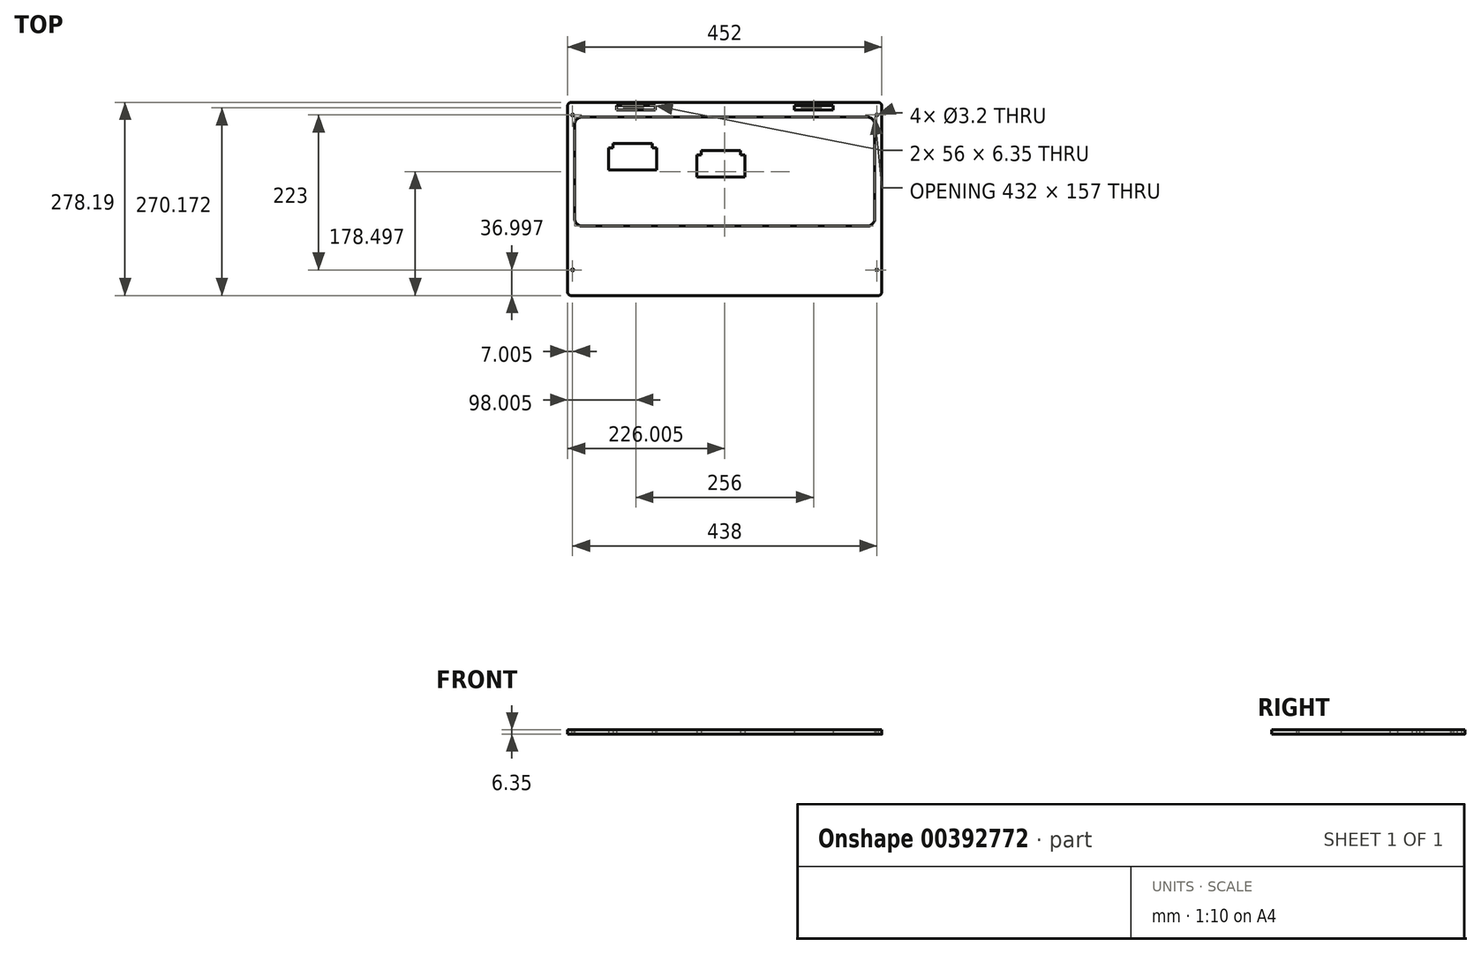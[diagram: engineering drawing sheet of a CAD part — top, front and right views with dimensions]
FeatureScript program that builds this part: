
annotation { "Feature Type Name" : "Feature", "Feature Type Description" : "" }
export const myFeature = defineFeature(function(context is Context, id is Id, definition is map)
    precondition{}
    {
        {
            var Q0;
            Q0=qCreatedBy(makeId("Top.planeOp"),FACE);
            var sketch = newSketch(context, id + "F0", { "sketchPlane" : qUnion([Q0])});
            skCircle(sketch, "E0", {"center": v(-221.69, 47.13) * mm, "radius": 1.6 * mm});
            skLineSegment(sketch, "E1", {"start": v(223.31, 49.13) * mm, "end": v(223.31, -177.87) * mm});
            skLineSegment(sketch, "E2", {"start": v(223.31, 49.13) * mm, "end": v(223.31, 47.13) * mm});
            skCircle(sketch, "E3", {"center": v(216.31, 47.13) * mm, "radius": 1.6 * mm});
            skLineSegment(sketch, "E4", {"start": v(223.31, -177.87) * mm, "end": v(223.31, -175.87) * mm});
            skLineSegment(sketch, "E5", {"start": v(-228.69, -177.87) * mm, "end": v(-228.69, -175.87) * mm});
            skCircle(sketch, "E6", {"center": v(-221.69, -175.87) * mm, "radius": 1.6 * mm});
            skCircle(sketch, "E7", {"center": v(216.31, -175.87) * mm, "radius": 1.6 * mm});
            skLineSegment(sketch, "E8", {"start": v(213.31, -31.18) * mm, "end": v(213.31, -101.87) * mm});
            skLineSegment(sketch, "E9", {"start": v(213.31, -31.18) * mm, "end": v(213.31, 33.13) * mm});
            skLineSegment(sketch, "E10", {"start": v(-207.69, -112.87) * mm, "end": v(202.31, -112.87) * mm});
            skLineSegment(sketch, "E11", {"start": v(-218.69, -34.37) * mm, "end": v(-218.69, -101.87) * mm});
            skLineSegment(sketch, "E12", {"start": v(-218.69, -34.37) * mm, "end": v(-218.69, 33.13) * mm});
            skLineSegment(sketch, "E13", {"start": v(-218.69, 33.13) * mm, "end": v(-218.69, 33.13) * mm});
            skArc(sketch, "E14.filletArc", {"start": v(-207.69, 44.13) * mm, "mid": v(-215.46, 40.9) * mm, "end": v(-218.69, 33.13) * mm});
            skArc(sketch, "E15.MirrorCS", {"start": v(202.31, 44.13) * mm, "mid": v(210.1, 40.9) * mm, "end": v(213.31, 33.13) * mm});
            skArc(sketch, "E16.MirrorCS", {"start": v(-207.69, -112.87) * mm, "mid": v(-215.46, -109.65) * mm, "end": v(-218.69, -101.87) * mm});
            skArc(sketch, "E17.MirrorCS", {"start": v(202.31, -112.87) * mm, "mid": v(210.1, -109.65) * mm, "end": v(213.31, -101.87) * mm});
            skPoint(sketch, "E18.start.orphan", {"position": v(-2.69, -112.87) * mm});
            skLineSegment(sketch, "E19", {"start": v(-64.45, -212.87) * mm, "end": v(-223.69, -212.87) * mm});
            skLineSegment(sketch, "E20", {"start": v(-228.69, -175.87) * mm, "end": v(-228.69, -207.87) * mm});
            skLineSegment(sketch, "E21", {"start": v(223.31, -177.87) * mm, "end": v(223.31, -207.87) * mm});
            skLineSegment(sketch, "E22", {"start": v(-64.45, -212.87) * mm, "end": v(218.31, -212.87) * mm});
            skLineSegment(sketch, "E23", {"start": v(223.31, -207.87) * mm, "end": v(223.31, -207.87) * mm});
            skLineSegment(sketch, "E24", {"start": v(218.31, -212.87) * mm, "end": v(218.31, -212.87) * mm});
            skArc(sketch, "E25.filletArc", {"start": v(218.31, -212.87) * mm, "mid": v(221.85, -211.4) * mm, "end": v(223.31, -207.87) * mm});
            skLineSegment(sketch, "E26", {"start": v(-228.69, -207.87) * mm, "end": v(-228.69, -207.87) * mm});
            skLineSegment(sketch, "E27", {"start": v(-223.69, -212.87) * mm, "end": v(-223.69, -212.87) * mm});
            skArc(sketch, "E28.filletArc", {"start": v(-228.69, -207.87) * mm, "mid": v(-227.22, -211.4) * mm, "end": v(-223.69, -212.87) * mm});
            skPoint(sketch, "E29.end.orphan", {"position": v(-218.69, -212.87) * mm});
            skLineSegment(sketch, "E30", {"start": v(-118.9, 65.32) * mm, "end": v(-223.69, 65.32) * mm});
            skLineSegment(sketch, "E31", {"start": v(-118.9, 65.32) * mm, "end": v(218.31, 65.32) * mm});
            skLineSegment(sketch, "E32", {"start": v(223.31, 47.13) * mm, "end": v(223.31, 60.48) * mm});
            skLineSegment(sketch, "E33", {"start": v(-158.69, 60.48) * mm, "end": v(-102.69, 60.48) * mm});
            skLineSegment(sketch, "E34", {"start": v(-207.69, 44.13) * mm, "end": v(202.31, 44.13) * mm});
            skLineSegment(sketch, "E35", {"start": v(-158.69, 60.48) * mm, "end": v(-158.69, 54.13) * mm});
            skLineSegment(sketch, "E36", {"start": v(-102.69, 60.48) * mm, "end": v(-102.69, 54.13) * mm});
            skLineSegment(sketch, "E37.trimOffspring", {"start": v(-158.69, 54.13) * mm, "end": v(-102.69, 54.13) * mm});
            skLineSegment(sketch, "E38", {"start": v(97.31, 60.48) * mm, "end": v(97.31, 54.13) * mm});
            skLineSegment(sketch, "E39", {"start": v(153.31, 60.48) * mm, "end": v(153.31, 54.13) * mm});
            skLineSegment(sketch, "E40.trimOffspring", {"start": v(153.31, 54.13) * mm, "end": v(97.31, 54.13) * mm});
            skLineSegment(sketch, "E41.trimOffspring", {"start": v(97.31, 54.13) * mm, "end": v(153.31, 54.13) * mm});
            skLineSegment(sketch, "E42.trimOffspring", {"start": v(97.31, 60.48) * mm, "end": v(153.31, 60.48) * mm});
            skLineSegment(sketch, "E43.trimOffspring", {"start": v(-102.69, 54.13) * mm, "end": v(-158.69, 54.13) * mm});
            skLineSegment(sketch, "E44.trimOffspring", {"start": v(-228.69, -175.87) * mm, "end": v(-228.69, -177.87) * mm});
            skLineSegment(sketch, "E45", {"start": v(-228.69, 60.32) * mm, "end": v(-228.69, -175.87) * mm});
            skLineSegment(sketch, "E46", {"start": v(-228.69, 60.32) * mm, "end": v(-228.69, 60.32) * mm});
            skPoint(sketch, "E47.newPointA", {"position": v(-228.69, 65.32) * mm});
            skArc(sketch, "E47.filletArc", {"start": v(-223.69, 65.32) * mm, "mid": v(-227.22, 63.86) * mm, "end": v(-228.69, 60.32) * mm});
            skArc(sketch, "E48.MirrorCS", {"start": v(218.31, 65.32) * mm, "mid": v(221.85, 63.86) * mm, "end": v(223.31, 60.32) * mm});
            skLineSegment(sketch, "E49.trimOffspring", {"start": v(223.31, 60.48) * mm, "end": v(223.31, 60.48) * mm});
            skPoint(sketch, "E50.start.orphan", {"position": v(-2.69, 44.13) * mm});
            skLineSegment(sketch, "E51.bottom", {"start": v(-163.3, 6.35) * mm, "end": v(-106.8, 6.35) * mm});
            skLineSegment(sketch, "E51.left", {"start": v(-163.3, 6.35) * mm, "end": v(-163.3, 0) * mm});
            skLineSegment(sketch, "E51.right", {"start": v(-106.8, 6.35) * mm, "end": v(-106.8, 0) * mm});
            skLineSegment(sketch, "E52.top", {"start": v(-163.3, -31.75) * mm, "end": v(-107.3, -31.75) * mm});
            skLineSegment(sketch, "E53", {"start": v(-163.3, 0) * mm, "end": v(-169.66, 0) * mm});
            skLineSegment(sketch, "E54", {"start": v(-169.66, 0) * mm, "end": v(-169.66, -31.75) * mm});
            skLineSegment(sketch, "E55", {"start": v(-169.66, -31.75) * mm, "end": v(-163.3, -31.75) * mm});
            skLineSegment(sketch, "E56", {"start": v(-106.8, 0) * mm, "end": v(-100.46, 0) * mm});
            skLineSegment(sketch, "E57", {"start": v(-100.46, 0) * mm, "end": v(-100.46, -31.75) * mm});
            skLineSegment(sketch, "E58", {"start": v(-100.46, -31.75) * mm, "end": v(-107.3, -31.75) * mm});
            skLineSegment(sketch, "E59.bottom", {"start": v(-36.24, -4.23) * mm, "end": v(19.76, -4.23) * mm});
            skLineSegment(sketch, "E59.left", {"start": v(-36.24, -4.23) * mm, "end": v(-36.24, -10.58) * mm});
            skLineSegment(sketch, "E59.right", {"start": v(19.76, -4.23) * mm, "end": v(19.76, -10.58) * mm});
            skLineSegment(sketch, "E60.top", {"start": v(-36.24, -42.33) * mm, "end": v(19.76, -42.33) * mm});
            skLineSegment(sketch, "E61", {"start": v(-36.24, -10.58) * mm, "end": v(-42.6, -10.58) * mm});
            skLineSegment(sketch, "E62", {"start": v(-42.6, -10.58) * mm, "end": v(-42.6, -42.33) * mm});
            skLineSegment(sketch, "E63", {"start": v(-42.6, -42.33) * mm, "end": v(-36.24, -42.33) * mm});
            skLineSegment(sketch, "E64", {"start": v(19.76, -10.58) * mm, "end": v(26.1, -10.58) * mm});
            skLineSegment(sketch, "E65", {"start": v(26.1, -10.58) * mm, "end": v(26.1, -42.33) * mm});
            skLineSegment(sketch, "E66", {"start": v(26.1, -42.33) * mm, "end": v(19.76, -42.33) * mm});
            skSolve(sketch);
        }
        {
            var Q0;
            Q0=makeQuery(id+"F0.imprint","IMPRINT",FACE,{"disambiguationData":[TD([[makeQuery(id+"F0.imprint","IMPRINT",EDGE,{"derivedFrom":sQuery(id+"F0.wireOp",EDGE,"E0")}),-1.0]])]});
            var Q1;
            Q1=makeQuery(id+"F0.imprint","IMPRINT",FACE,{"disambiguationData":[TD([[makeQuery(id+"F0.imprint","IMPRINT",EDGE,{"derivedFrom":sQuery(id+"F0.wireOp",EDGE,"E51.bottom")}),-1.0]])]});
            var Q2;
            Q2=makeQuery(id+"F0.imprint","IMPRINT",FACE,{"disambiguationData":[TD([[makeQuery(id+"F0.imprint","IMPRINT",EDGE,{"derivedFrom":sQuery(id+"F0.wireOp",EDGE,"E59.bottom")}),-1.0]])]});
            extrude(context, id + "F1", {"entities" : qUnion([Q0, Q1, Q2]), "depth" : 6.35 * mm});
        }
    });
